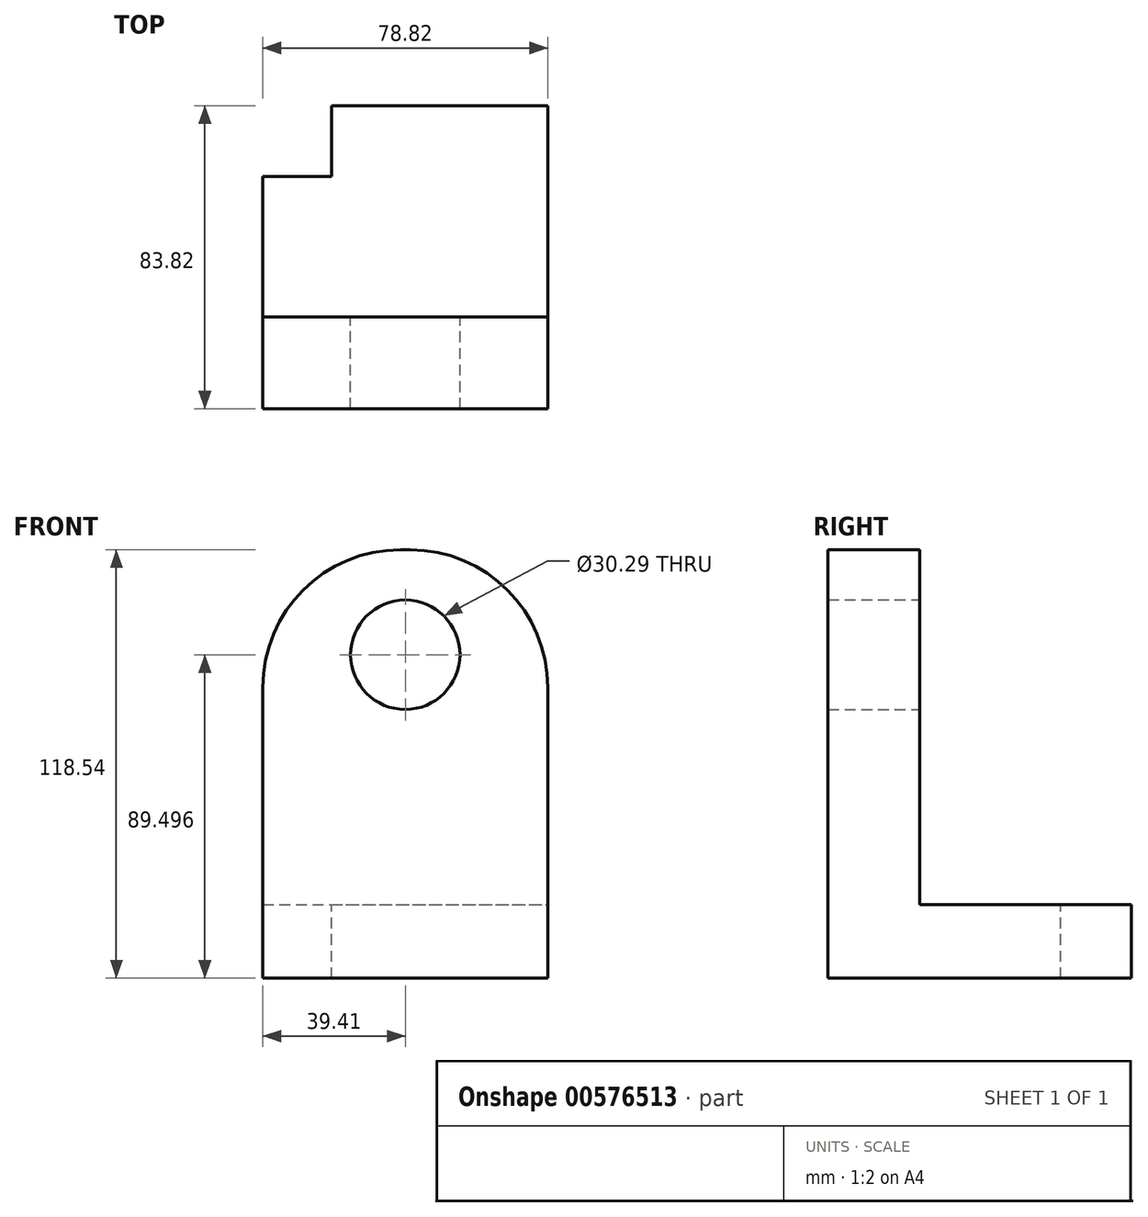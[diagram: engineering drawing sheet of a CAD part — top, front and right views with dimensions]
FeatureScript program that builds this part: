
annotation { "Feature Type Name" : "Feature", "Feature Type Description" : "" }
export const myFeature = defineFeature(function(context is Context, id is Id, definition is map)
    precondition{}
    {
        {
            var Q0;
            Q0=qCreatedBy(makeId("Front.planeOp"),FACE);
            var sketch = newSketch(context, id + "F0", { "sketchPlane" : qUnion([Q0])});
            skLineSegment(sketch, "E0.bottom", {"start": v(-39.41, 59.27) * mm, "end": v(39.41, 59.27) * mm});
            skLineSegment(sketch, "E0.top", {"start": v(-39.41, -59.27) * mm, "end": v(39.41, -59.27) * mm});
            skLineSegment(sketch, "E0.left", {"start": v(-39.41, 59.27) * mm, "end": v(-39.41, -59.27) * mm});
            skLineSegment(sketch, "E0.right", {"start": v(39.41, 59.27) * mm, "end": v(39.41, -59.27) * mm});
            skPoint(sketch, "E0.middle", {"position": v(0, 0) * mm});
            skSolve(sketch);
        }
        {
            var Q0;
            Q0=makeQuery(id+"F0.imprint","IMPRINT",FACE,{"disambiguationData":[TD([[makeQuery(id+"F0.imprint","IMPRINT",EDGE,{"derivedFrom":sQuery(id+"F0.wireOp",EDGE,"E0.bottom")}),-1.0]])]});
            extrude(context, id + "F1", {"entities" : qUnion([Q0]), "depth" : 25.4 * mm, "offsetDistance" : 25.4 * mm});
        }
        {
            var Q0;
            Q0=makeQuery(id+"F1.opExtrude","SWEPT_EDGE",EDGE,{"disambiguationData":[OSD([sQuery(id+"F0.wireOp",EDGE,"E0.bottom"),sQuery(id+"F0.wireOp",EDGE,"E0.left")])]});
            var Q1;
            Q1=makeQuery(id+"F1.opExtrude","SWEPT_EDGE",EDGE,{"disambiguationData":[OSD([sQuery(id+"F0.wireOp",EDGE,"E0.bottom"),sQuery(id+"F0.wireOp",EDGE,"E0.right")])]});
            fillet(context, id + "F2", {"entities" : qUnion([Q0, Q1]), "radius" : 38.1 * mm, "tangentPropagation" : true, "allowEdgeOverflow" : false});
        }
        {
            var Q0;
            Q0=qCreatedBy(makeId("Front.planeOp"),FACE);
            var sketch = newSketch(context, id + "F3", { "sketchPlane" : qUnion([Q0])});
            skCircle(sketch, "E1", {"center": v(0, 30.23) * mm, "radius": 15.14 * mm});
            skSolve(sketch);
        }
        {
            var Q0;
            Q0=makeQuery(id+"F3.imprint","IMPRINT",FACE,{"disambiguationData":[TD([[makeQuery(id+"F3.imprint","IMPRINT",EDGE,{"derivedFrom":sQuery(id+"F3.wireOp",EDGE,"E1")}),1.0]])]});
            extrude(context, id + "F4", {"entities" : qUnion([Q0]), "operationType" : NewBodyOperationType.REMOVE, "endBound" : BoundingType.THROUGH_ALL, "depth" : 25.4 * mm, "offsetDistance" : 25.4 * mm});
        }
        {
            var Q0;
            Q0=qCreatedBy(makeId("Front.planeOp"),FACE);
            var sketch = newSketch(context, id + "F5", { "sketchPlane" : qUnion([Q0])});
            skLineSegment(sketch, "E2.bottom", {"start": v(-39.41, -59.27) * mm, "end": v(39.41, -59.27) * mm});
            skLineSegment(sketch, "E2.top", {"start": v(-39.41, -38.92) * mm, "end": v(39.41, -38.92) * mm});
            skLineSegment(sketch, "E2.left", {"start": v(-39.41, -59.27) * mm, "end": v(-39.41, -38.92) * mm});
            skLineSegment(sketch, "E2.right", {"start": v(39.41, -59.27) * mm, "end": v(39.41, -38.92) * mm});
            skPoint(sketch, "E2.middle", {"position": v(0, -49.1) * mm});
            skSolve(sketch);
        }
        {
            var Q0;
            Q0 = qSketchRegion(id + "F5", true);
            var Q1;
            Q1 = qConstructionFilter(qBodyType(qCreatedBy(id + "F5" ,EDGE), BodyType.WIRE), ConstructionObject.NO);
            extrude(context, id + "F6", {"entities" : qUnion([Q0]), "operationType" : NewBodyOperationType.ADD, "surfaceEntities" : qUnion([Q1]), "oppositeDirection" : true, "depth" : 58.42 * mm, "offsetDistance" : 25.4 * mm});
        }
        {
            var Q0;
            Q0=makeQuery(id+"F6.opExtrude","CAP_FACE",FACE,{"disambiguationData":[OSD([sQuery(id+"F5.wireOp",EDGE,"E2.bottom"),sQuery(id+"F5.wireOp",EDGE,"E2.top"),sQuery(id+"F5.wireOp",EDGE,"E2.left"),sQuery(id+"F5.wireOp",EDGE,"E2.right")])],"isStart":false});
            var sketch = newSketch(context, id + "F7", { "sketchPlane" : qUnion([Q0])});
            skLineSegment(sketch, "E3.bottom", {"start": v(39.41, -59.27) * mm, "end": v(20.36, -59.27) * mm});
            skLineSegment(sketch, "E3.top", {"start": v(39.41, -38.92) * mm, "end": v(20.36, -38.92) * mm});
            skLineSegment(sketch, "E3.left", {"start": v(39.41, -59.27) * mm, "end": v(39.41, -38.92) * mm});
            skLineSegment(sketch, "E3.right", {"start": v(20.36, -59.27) * mm, "end": v(20.36, -38.92) * mm});
            skSolve(sketch);
        }
        {
            var Q0;
            Q0 = qSketchRegion(id + "F7", true);
            extrude(context, id + "F8", {"entities" : qUnion([Q0]), "operationType" : NewBodyOperationType.REMOVE, "oppositeDirection" : true, "depth" : 19.56 * mm, "offsetDistance" : 25.4 * mm});
        }
    });
